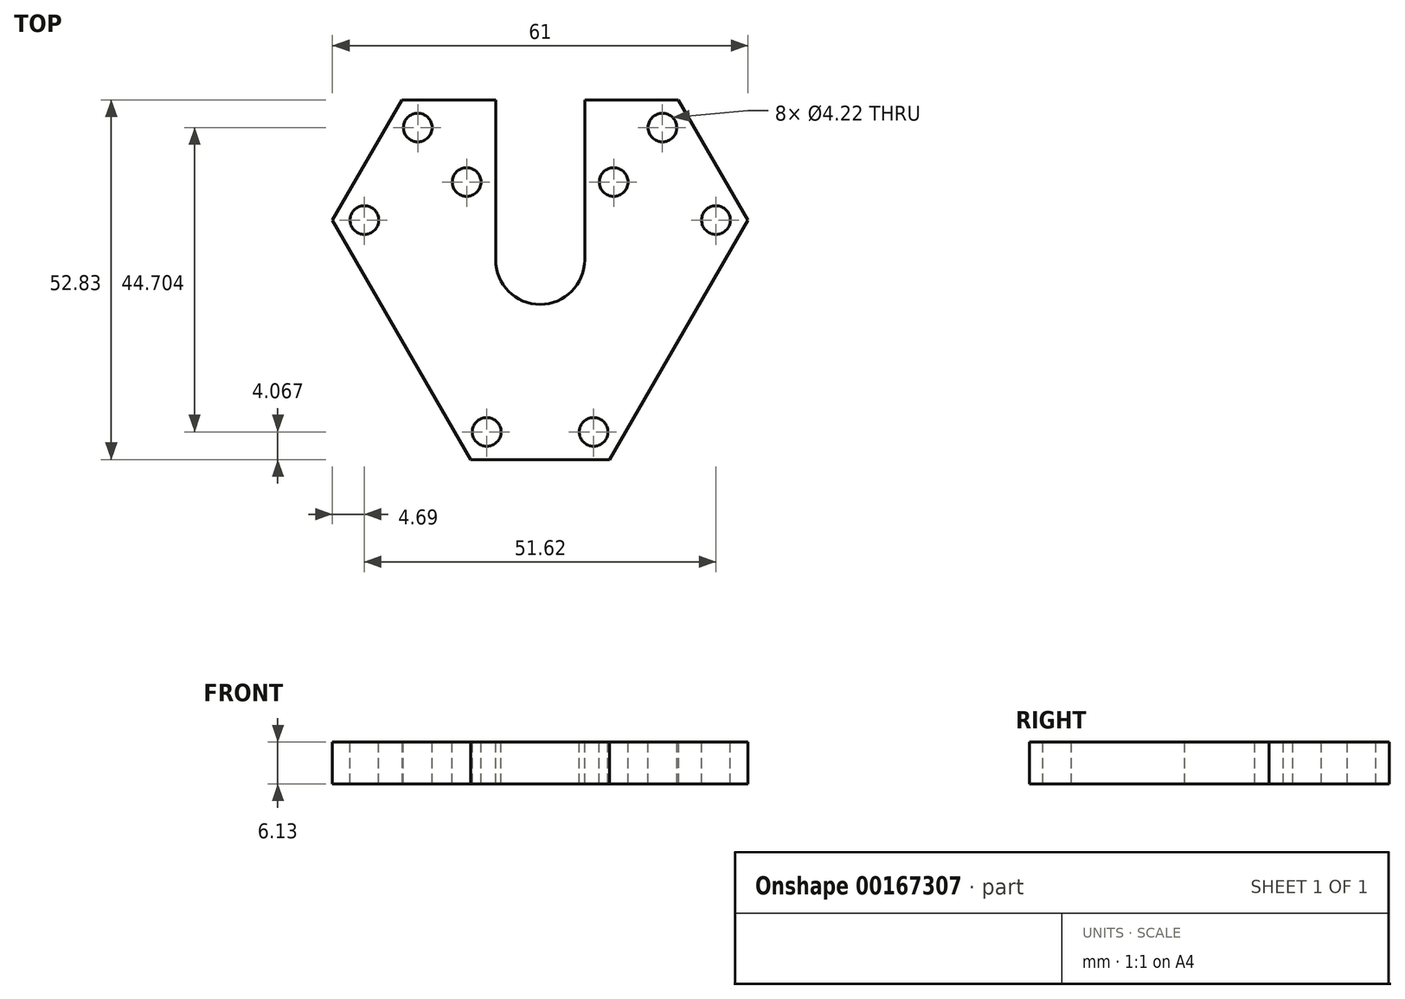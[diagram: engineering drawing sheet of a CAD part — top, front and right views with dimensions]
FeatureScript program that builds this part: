
annotation { "Feature Type Name" : "Feature", "Feature Type Description" : "" }
export const myFeature = defineFeature(function(context is Context, id is Id, definition is map)
    precondition{}
    {
        {
            var Q0;
            Q0=qCreatedBy(makeId("Top.planeOp"),FACE);
            var sketch = newSketch(context, id + "F0", { "sketchPlane" : qUnion([Q0])});
            skLineSegment(sketch, "E0", {"start": v(-10.2, -29.34) * mm, "end": v(10.2, -29.34) * mm});
            skLineSegment(sketch, "E1", {"start": v(10.2, -29.34) * mm, "end": v(30.5, 5.84) * mm});
            skLineSegment(sketch, "E2", {"start": v(30.5, 5.84) * mm, "end": v(20.31, 23.5) * mm});
            skLineSegment(sketch, "E3", {"start": v(20.31, 23.5) * mm, "end": v(-20.31, 23.5) * mm});
            skLineSegment(sketch, "E4", {"start": v(-20.31, 23.5) * mm, "end": v(-30.5, 5.84) * mm});
            skLineSegment(sketch, "E5", {"start": v(-30.5, 5.84) * mm, "end": v(-10.2, -29.34) * mm});
            skSolve(sketch);
        }
        {
            var Q0;
            Q0 = qSketchRegion(id + "F0", true);
            extrude(context, id + "F1", {"entities" : qUnion([Q0]), "depth" : 6.13 * mm});
        }
        {
            var Q0;
            Q0=makeQuery(id+"F1.opExtrude","CAP_FACE",FACE,{"disambiguationData":[OSD([sQuery(id+"F0.wireOp",EDGE,"E0"),sQuery(id+"F0.wireOp",EDGE,"E1"),sQuery(id+"F0.wireOp",EDGE,"E2"),sQuery(id+"F0.wireOp",EDGE,"E3"),sQuery(id+"F0.wireOp",EDGE,"E4"),sQuery(id+"F0.wireOp",EDGE,"E5")])],"isStart":false});
            var sketch = newSketch(context, id + "F2", { "sketchPlane" : qUnion([Q0])});
            skLineSegment(sketch, "E6", {"start": v(-7.85, -25.27) * mm, "end": v(7.85, -25.27) * mm});
            skLineSegment(sketch, "E7", {"start": v(-7.85, -25.27) * mm, "end": v(-25.8, 5.84) * mm});
            skLineSegment(sketch, "E8", {"start": v(-25.8, 5.84) * mm, "end": v(-17.96, 19.43) * mm});
            skLineSegment(sketch, "E9", {"start": v(-17.96, 19.43) * mm, "end": v(17.96, 19.43) * mm});
            skLineSegment(sketch, "E10", {"start": v(17.96, 19.43) * mm, "end": v(25.8, 5.84) * mm});
            skLineSegment(sketch, "E11", {"start": v(25.8, 5.84) * mm, "end": v(7.85, -25.27) * mm});
            skSolve(sketch);
        }
        {
            var Q0;
            Q0=sQuery(id+"F2.wireOp",VERTEX,"E9.start");
            var Q1;
            Q1=sQuery(id+"F2.wireOp",VERTEX,"E8.start");
            var Q2;
            Q2=sQuery(id+"F2.wireOp",VERTEX,"E7.start");
            var Q3;
            Q3=sQuery(id+"F2.wireOp",VERTEX,"E6.end");
            var Q4;
            Q4=sQuery(id+"F2.wireOp",VERTEX,"E11.start");
            var Q5;
            Q5=sQuery(id+"F2.wireOp",VERTEX,"E10.start");
            var Q6;
            Q6=makeQuery(id+"F1.opExtrude","SWEPT_BODY",BODY,{"disambiguationData":[OSD([sQuery(id+"F0.wireOp",EDGE,"E0"),sQuery(id+"F0.wireOp",EDGE,"E1"),sQuery(id+"F0.wireOp",EDGE,"E2"),sQuery(id+"F0.wireOp",EDGE,"E3"),sQuery(id+"F0.wireOp",EDGE,"E4"),sQuery(id+"F0.wireOp",EDGE,"E5")])]});
            hole(context, id + "F3", {"style" : HoleStyle.SIMPLE, "endStyle" : HoleEndStyle.THROUGH, "holeDiameter" : 4.22 * mm, "locations" : qUnion([Q0, Q1, Q2, Q3, Q4, Q5]), "scope" : qUnion([Q6]), "isTappedThrough" : true});
        }
        {
            var Q0;
            Q0=makeQuery(id+"F1.opExtrude","CAP_FACE",FACE,{"disambiguationData":[OSD([sQuery(id+"F0.wireOp",EDGE,"E0"),sQuery(id+"F0.wireOp",EDGE,"E1"),sQuery(id+"F0.wireOp",EDGE,"E2"),sQuery(id+"F0.wireOp",EDGE,"E3"),sQuery(id+"F0.wireOp",EDGE,"E4"),sQuery(id+"F0.wireOp",EDGE,"E5")])],"isStart":false});
            var sketch = newSketch(context, id + "F4", { "sketchPlane" : qUnion([Q0])});
            skArc(sketch, "E12", {"start": v(-6.54, 0) * mm, "mid": v(0, -6.54) * mm, "end": v(6.54, 0) * mm});
            skLineSegment(sketch, "E13", {"start": v(-6.54, 0) * mm, "end": v(-6.54, 23.5) * mm});
            skLineSegment(sketch, "E14", {"start": v(6.54, 0) * mm, "end": v(6.54, 23.5) * mm});
            skLineSegment(sketch, "E15", {"start": v(6.54, 23.5) * mm, "end": v(-6.54, 23.5) * mm});
            skSolve(sketch);
        }
        {
            var Q0;
            Q0 = qSketchRegion(id + "F4", true);
            extrude(context, id + "F5", {"entities" : qUnion([Q0]), "operationType" : NewBodyOperationType.REMOVE, "endBound" : BoundingType.UP_TO_NEXT, "oppositeDirection" : true, "depth" : 25.4 * mm});
        }
        {
            var Q0;
            Q0=makeQuery(id+"F1.opExtrude","CAP_FACE",FACE,{"disambiguationData":[OSD([sQuery(id+"F0.wireOp",EDGE,"E0"),sQuery(id+"F0.wireOp",EDGE,"E1"),sQuery(id+"F0.wireOp",EDGE,"E2"),sQuery(id+"F0.wireOp",EDGE,"E3"),sQuery(id+"F0.wireOp",EDGE,"E4"),sQuery(id+"F0.wireOp",EDGE,"E5")])],"isStart":false});
            var sketch = newSketch(context, id + "F6", { "sketchPlane" : qUnion([Q0])});
            skLineSegment(sketch, "E16", {"start": v(-10.8, 11.43) * mm, "end": v(10.8, 11.43) * mm});
            skSolve(sketch);
        }
        {
            var Q0;
            Q0=sQuery(id+"F6.wireOp",VERTEX,"E16.start");
            var Q1;
            Q1=sQuery(id+"F6.wireOp",VERTEX,"E16.end");
            var Q2;
            Q2=makeQuery(id+"F1.opExtrude","SWEPT_BODY",BODY,{"disambiguationData":[OSD([sQuery(id+"F0.wireOp",EDGE,"E0"),sQuery(id+"F0.wireOp",EDGE,"E1"),sQuery(id+"F0.wireOp",EDGE,"E2"),sQuery(id+"F0.wireOp",EDGE,"E3"),sQuery(id+"F0.wireOp",EDGE,"E4"),sQuery(id+"F0.wireOp",EDGE,"E5")])]});
            hole(context, id + "F7", {"style" : HoleStyle.SIMPLE, "endStyle" : HoleEndStyle.THROUGH, "holeDiameter" : 4.22 * mm, "locations" : qUnion([Q0, Q1]), "scope" : qUnion([Q2]), "isTappedThrough" : true});
        }
    });
